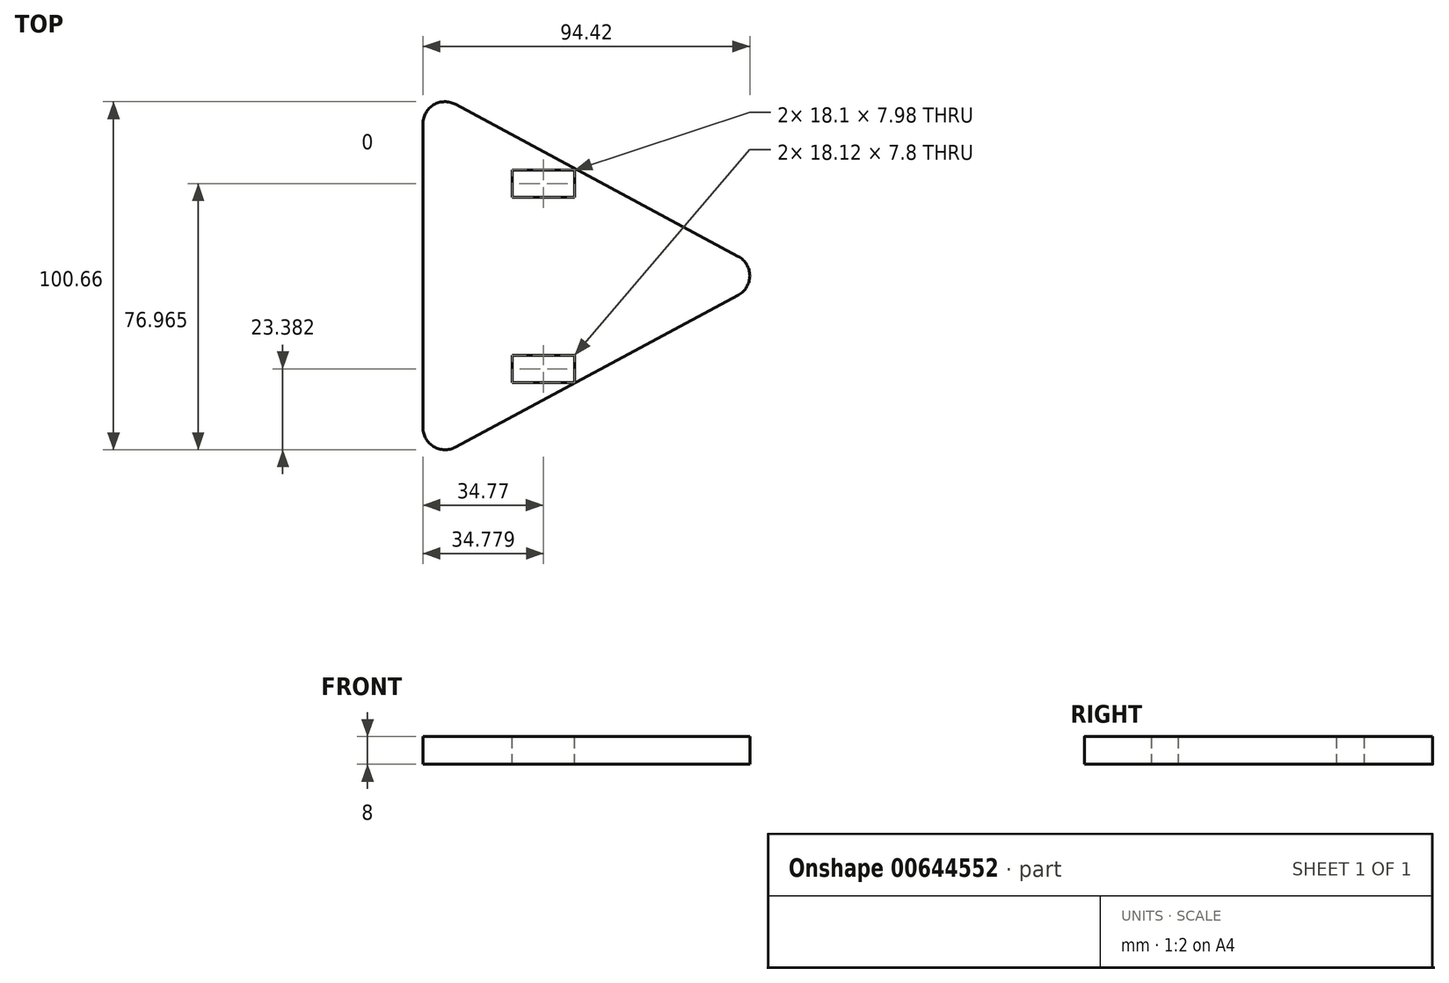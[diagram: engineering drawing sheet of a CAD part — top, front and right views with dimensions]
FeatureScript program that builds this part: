
annotation { "Feature Type Name" : "Feature", "Feature Type Description" : "" }
export const myFeature = defineFeature(function(context is Context, id is Id, definition is map)
    precondition{}
    {
        {
            var Q0;
            Q0=qCreatedBy(makeId("Top.planeOp"),FACE);
            var sketch = newSketch(context, id + "F0", { "sketchPlane" : qUnion([Q0])});
            skLineSegment(sketch, "E0", {"start": v(54.55, 5.6) * mm, "end": v(-27.18, 49.57) * mm});
            skLineSegment(sketch, "E1", {"start": v(54.55, -5.6) * mm, "end": v(-27.18, -49.57) * mm});
            skLineSegment(sketch, "E2", {"start": v(-36.53, 43.98) * mm, "end": v(-36.53, -43.98) * mm});
            skPoint(sketch, "E3.visualSharp", {"position": v(64.94, 0) * mm});
            skArc(sketch, "E3.filletArc", {"start": v(54.55, -5.6) * mm, "mid": v(57.89, 0) * mm, "end": v(54.55, 5.6) * mm});
            skPoint(sketch, "E4.visualSharp", {"position": v(-36.53, 54.6) * mm});
            skArc(sketch, "E4.filletArc", {"start": v(-27.18, 49.57) * mm, "mid": v(-33.44, 49.43) * mm, "end": v(-36.53, 43.98) * mm});
            skPoint(sketch, "E5.visualSharp", {"position": v(-36.53, -54.6) * mm});
            skArc(sketch, "E5.filletArc", {"start": v(-36.53, -43.98) * mm, "mid": v(-33.44, -49.43) * mm, "end": v(-27.18, -49.57) * mm});
            skSolve(sketch);
        }
        {
            var Q0;
            Q0=makeQuery(id+"F0.imprint","IMPRINT",FACE,{"disambiguationData":[TD([[makeQuery(id+"F0.imprint","IMPRINT",EDGE,{"derivedFrom":sQuery(id+"F0.wireOp",EDGE,"E0")}),1.0]])]});
            extrude(context, id + "F1", {"entities" : qUnion([Q0]), "depth" : 8 * mm, "offsetDistance" : 25 * mm});
        }
        {
            var Q0;
            Q0=makeQuery(id+"F1.opExtrude","CAP_FACE",FACE,{"disambiguationData":[OSD([sQuery(id+"F0.wireOp",EDGE,"E0"),sQuery(id+"F0.wireOp",EDGE,"E1"),sQuery(id+"F0.wireOp",EDGE,"E2"),sQuery(id+"F0.wireOp",EDGE,"E3.filletArc"),sQuery(id+"F0.wireOp",EDGE,"E4.filletArc"),sQuery(id+"F0.wireOp",EDGE,"E5.filletArc")])],"isStart":false});
            var sketch = newSketch(context, id + "F2", { "sketchPlane" : qUnion([Q0])});
            skLineSegment(sketch, "E6", {"start": v(-10.8, 40.76) * mm, "end": v(-10.8, -40.76) * mm});
            skLineSegment(sketch, "E7", {"start": v(7.39, 30.97) * mm, "end": v(7.39, -30.97) * mm});
            skSolve(sketch);
        }
        {
            var Q0;
            {var subQ0=sQuery(id+"F2.wireOp",EDGE,"E6");Q0=makeQuery(id+"F2.imprint","IMPRINT",FACE,{"disambiguationData":[TD([[makeQuery(id+"F2.imprint","IMPRINT",EDGE,{"derivedFrom":subQ0}),1.0]])]});}
            var sketch = newSketch(context, id + "F3", { "sketchPlane" : qUnion([Q0])});
            skLineSegment(sketch, "E8.bottom", {"start": v(7.29, 30.62) * mm, "end": v(-10.84, 30.62) * mm});
            skLineSegment(sketch, "E8.top", {"start": v(7.29, 22.65) * mm, "end": v(-10.84, 22.65) * mm});
            skLineSegment(sketch, "E8.left", {"start": v(7.29, 30.62) * mm, "end": v(7.29, 22.65) * mm});
            skLineSegment(sketch, "E8.right", {"start": v(-10.84, 30.62) * mm, "end": v(-10.84, 22.65) * mm});
            skSolve(sketch);
        }
        {
            var Q0;
            {var subQ1=sQuery(id+"F3.wireOp",EDGE,"E8.left");Q0=makeQuery(id+"F3.imprint","IMPRINT",FACE,{"disambiguationData":[TD([[makeQuery(id+"F3.imprint","IMPRINT",EDGE,{"derivedFrom":subQ1}),1.0]])]});}
            var sketch = newSketch(context, id + "F4", { "sketchPlane" : qUnion([Q0])});
            skLineSegment(sketch, "E9.bottom", {"start": v(7.3, -30.85) * mm, "end": v(-10.95, -30.85) * mm});
            skLineSegment(sketch, "E9.top", {"start": v(7.3, -23.05) * mm, "end": v(-10.95, -23.05) * mm});
            skLineSegment(sketch, "E9.left", {"start": v(7.3, -30.85) * mm, "end": v(7.3, -23.05) * mm});
            skLineSegment(sketch, "E9.right", {"start": v(-10.95, -30.85) * mm, "end": v(-10.95, -23.05) * mm});
            skSolve(sketch);
        }
        {
            var Q0;
            {var subQ0=sQuery(id+"F3.wireOp",EDGE,"E8.left");Q0=makeQuery(id+"F3.imprint","IMPRINT",FACE,{"disambiguationData":[TD([[makeQuery(id+"F3.imprint","IMPRINT",EDGE,{"derivedFrom":subQ0}),-1.0]])]});}
            extrude(context, id + "F5", {"entities" : qUnion([Q0]), "operationType" : NewBodyOperationType.REMOVE, "oppositeDirection" : true, "depth" : 8 * mm, "offsetDistance" : 25 * mm});
        }
        {
            var Q0;
            {var subQ0=sQuery(id+"F4.wireOp",EDGE,"E9.left");Q0=makeQuery(id+"F4.imprint","IMPRINT",FACE,{"disambiguationData":[TD([[makeQuery(id+"F4.imprint","IMPRINT",EDGE,{"derivedFrom":subQ0}),1.0]])]});}
            extrude(context, id + "F6", {"entities" : qUnion([Q0]), "operationType" : NewBodyOperationType.REMOVE, "oppositeDirection" : true, "depth" : 8 * mm, "offsetDistance" : 25 * mm});
        }
    });
